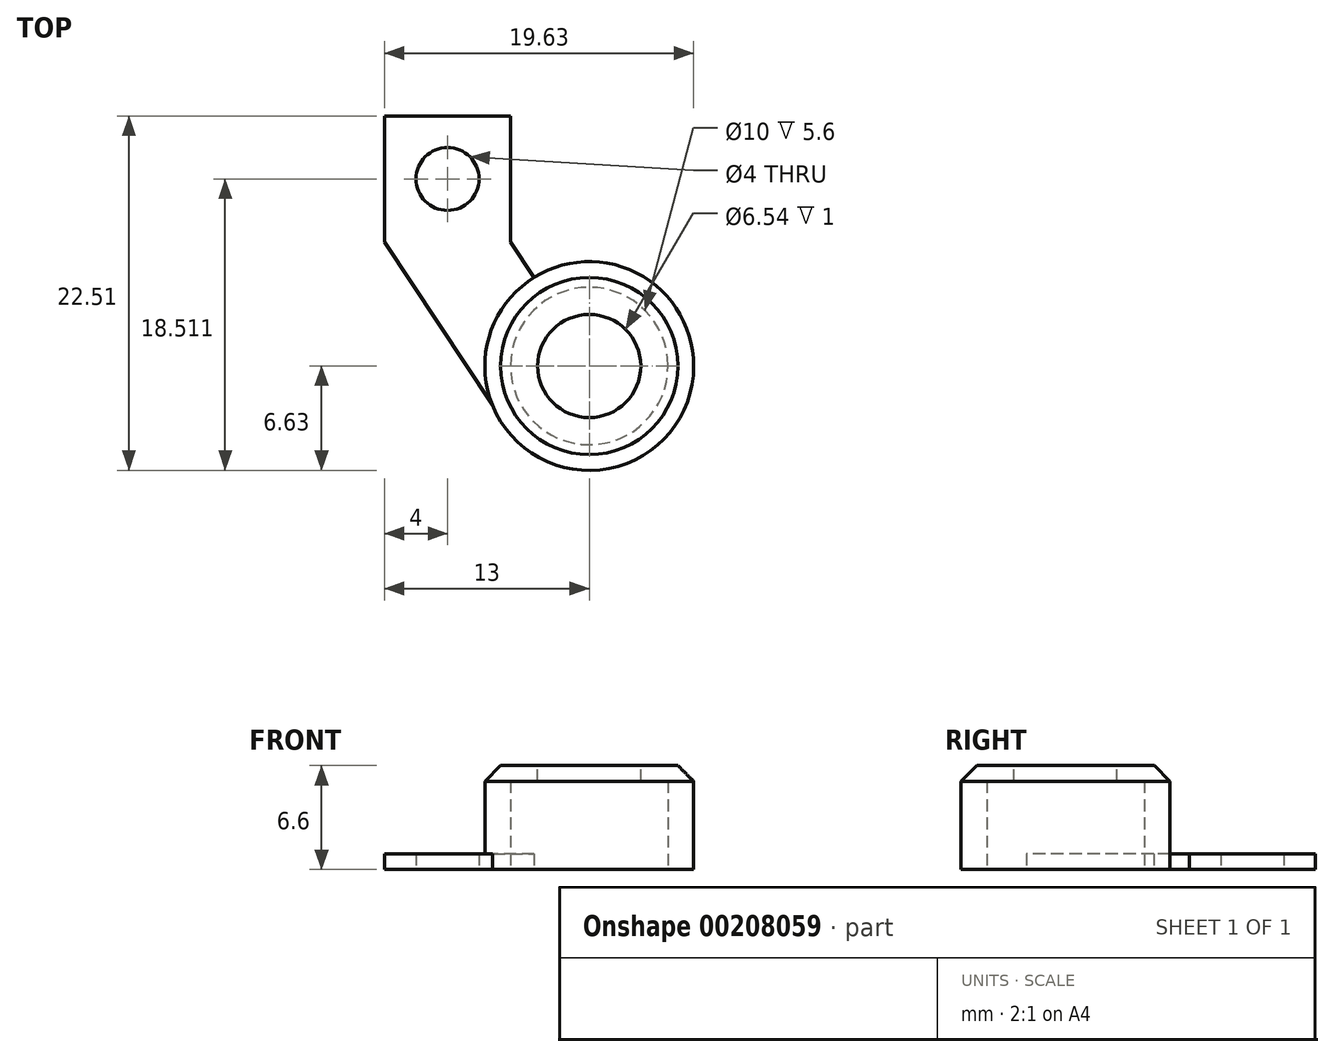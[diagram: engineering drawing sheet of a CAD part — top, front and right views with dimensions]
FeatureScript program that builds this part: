
annotation { "Feature Type Name" : "Feature", "Feature Type Description" : "" }
export const myFeature = defineFeature(function(context is Context, id is Id, definition is map)
    precondition{}
    {
        {
            var Q0;
            Q0=qCreatedBy(makeId("Top.planeOp"),FACE);
            var sketch = newSketch(context, id + "F0", { "sketchPlane" : qUnion([Q0])});
            skCircle(sketch, "E0", {"center": v(0, 0) * mm, "radius": 5 * mm});
            skCircle(sketch, "E1", {"center": v(0, 0) * mm, "radius": 6.63 * mm});
            skLineSegment(sketch, "E2.bottom", {"start": v(-13, 15.88) * mm, "end": v(-5, 15.88) * mm});
            skLineSegment(sketch, "E2.top", {"start": v(-13, 7.88) * mm, "end": v(-5, 7.88) * mm});
            skLineSegment(sketch, "E2.left", {"start": v(-13, 15.88) * mm, "end": v(-13, 7.88) * mm});
            skLineSegment(sketch, "E2.right", {"start": v(-5, 15.88) * mm, "end": v(-5, 7.88) * mm});
            skLineSegment(sketch, "E3", {"start": v(-13, 7.88) * mm, "end": v(-6.15, -2.47) * mm});
            skLineSegment(sketch, "E4", {"start": v(-5, 7.88) * mm, "end": v(-3.5, 5.63) * mm});
            skCircle(sketch, "E5", {"center": v(-9, 11.88) * mm, "radius": 2 * mm});
            skPoint(sketch, "E5.centerSnap0", {"position": v(-9, 15.88) * mm});
            skPoint(sketch, "E5.centerSnap1", {"position": v(-13, 11.88) * mm});
            skSolve(sketch);
        }
        {
            var Q0;
            Q0=makeQuery(id+"F0.imprint","IMPRINT",FACE,{"disambiguationData":[TD([[makeQuery(id+"F0.imprint","IMPRINT",EDGE,{"derivedFrom":sQuery(id+"F0.wireOp",EDGE,"E2.bottom")}),-1.0]])]});
            var Q1;
            Q1=makeQuery(id+"F0.imprint","IMPRINT",FACE,{"disambiguationData":[TD([[makeQuery(id+"F0.imprint","IMPRINT",EDGE,{"derivedFrom":sQuery(id+"F0.wireOp",EDGE,"E2.top")}),-1.0]])]});
            extrude(context, id + "F1", {"entities" : qUnion([Q0, Q1]), "depth" : 1 * mm});
        }
        {
            var Q0;
            Q0=makeQuery(id+"F0.imprint","IMPRINT",FACE,{"disambiguationData":[TD([[makeQuery(id+"F0.imprint","IMPRINT",EDGE,{"derivedFrom":sQuery(id+"F0.wireOp",EDGE,"E0")}),-1.0]])]});
            extrude(context, id + "F2", {"entities" : qUnion([Q0]), "operationType" : NewBodyOperationType.ADD, "depth" : 6.6 * mm});
        }
        {
            var Q0;
            Q0=makeQuery(id+"F2.opExtrude","CAP_FACE",FACE,{"disambiguationData":[OSD([sQuery(id+"F0.wireOp",EDGE,"E0"),sQuery(id+"F0.wireOp",EDGE,"E1")])],"isStart":false});
            var sketch = newSketch(context, id + "F3", { "sketchPlane" : qUnion([Q0])});
            skCircle(sketch, "E6", {"center": v(0, 0) * mm, "radius": 3.27 * mm});
            skSolve(sketch);
        }
        {
            var Q0;
            Q0=makeQuery(id+"F3.imprint","IMPRINT",FACE,{"disambiguationData":[TD([[makeQuery(id+"F3.imprint","IMPRINT",EDGE,{"derivedFrom":sQuery(id+"F3.wireOp",EDGE,"E6")}),-1.0]])]});
            extrude(context, id + "F4", {"entities" : qUnion([Q0]), "operationType" : NewBodyOperationType.ADD, "oppositeDirection" : true, "depth" : 1 * mm});
        }
        {
            var Q0;
            Q0=makeQuery(id+"F2.opExtrude","CAP_EDGE",EDGE,{"disambiguationData":[OSD([sQuery(id+"F0.wireOp",EDGE,"E1")])],"isStart":false});
            chamfer(context, id + "F5", {"entities" : qUnion([Q0]), "width" : 1 * mm, "tangentPropagation" : true});
        }
    });
